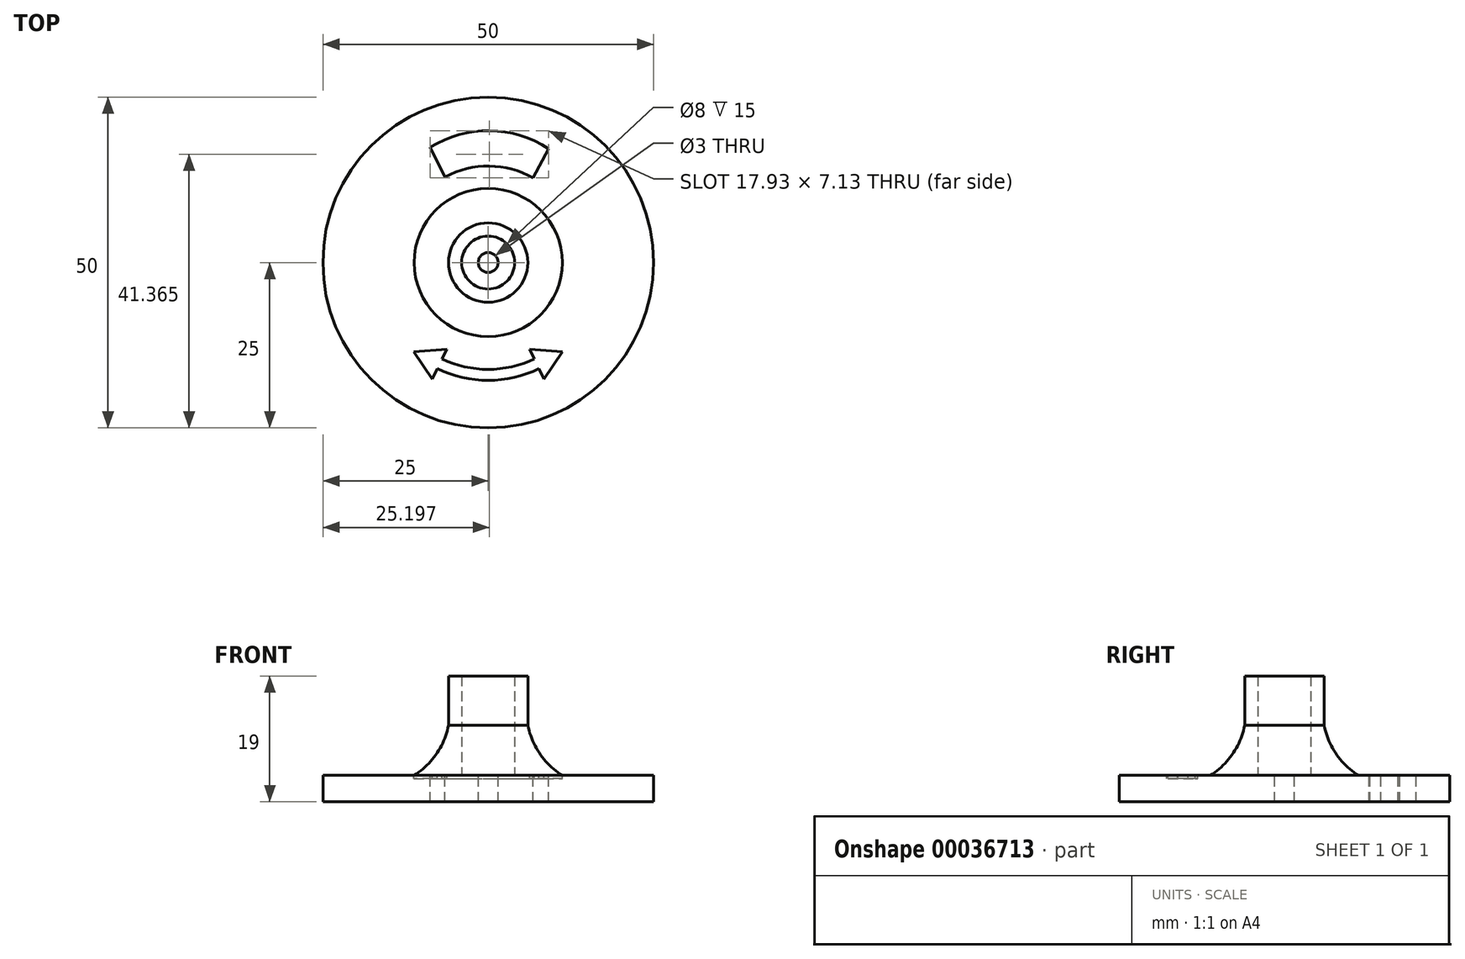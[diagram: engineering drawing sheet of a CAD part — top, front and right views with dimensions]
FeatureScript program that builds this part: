
annotation { "Feature Type Name" : "Feature", "Feature Type Description" : "" }
export const myFeature = defineFeature(function(context is Context, id is Id, definition is map)
    precondition{}
    {
        {
            var Q0;
            Q0=qCreatedBy(makeId("Top.planeOp"),FACE);
            var sketch = newSketch(context, id + "F0", { "sketchPlane" : qUnion([Q0])});
            skCircle(sketch, "E0", {"center": v(0, 0) * mm, "radius": 25 * mm});
            skSolve(sketch);
        }
        {
            var Q0;
            Q0=qCreatedBy(makeId("Top.planeOp"),FACE);
            var sketch = newSketch(context, id + "F1", { "sketchPlane" : qUnion([Q0])});
            skCircle(sketch, "E1", {"center": v(0, 0) * mm, "radius": 6 * mm});
            skCircle(sketch, "E2", {"center": v(0, 0) * mm, "radius": 4 * mm});
            skSolve(sketch);
        }
        {
            var Q0;
            Q0 = qSketchRegion(id + "F0", true);
            extrude(context, id + "F2", {"entities" : qUnion([Q0]), "depth" : 4 * mm});
        }
        {
            var Q0;
            Q0 = qSketchRegion(id + "F1", true);
            extrude(context, id + "F3", {"entities" : qUnion([Q0]), "operationType" : NewBodyOperationType.ADD, "depth" : 19 * mm});
        }
        {
            var Q0;
            {var subQ0=sQuery(id+"F0.wireOp",EDGE,"E0");Q0=makeQuery(id+"F3.boolean.opBoolean","SPLIT",FACE,{"disambiguationData":[TD([makeQuery(id+"F2.opExtrude","SWEPT_FACE",FACE,{"disambiguationData":[OSD([subQ0])]})])],"derivedFrom":makeQuery(id+"F2.opExtrude","CAP_FACE",FACE,{"disambiguationData":[OSD([subQ0])],"isStart":false})});}
            var sketch = newSketch(context, id + "F4", { "sketchPlane" : qUnion([Q0])});
            skCircle(sketch, "E3", {"center": v(0, 0) * mm, "radius": 1.5 * mm});
            skSolve(sketch);
        }
        {
            var Q0;
            Q0=makeQuery(id+"F4.imprint","IMPRINT",FACE,{"disambiguationData":[TD([[makeQuery(id+"F4.imprint","IMPRINT",EDGE,{"derivedFrom":sQuery(id+"F4.wireOp",EDGE,"E3")}),1.0]])]});
            var Q1;
            Q1=sQuery(id+"F4.wireOp",EDGE,"E3");
            extrude(context, id + "F5", {"entities" : qUnion([Q0]), "operationType" : NewBodyOperationType.REMOVE, "surfaceEntities" : qUnion([Q1]), "endBound" : BoundingType.THROUGH_ALL, "oppositeDirection" : true, "depth" : 10 * mm});
        }
        {
            var Q0;
            Q0=qCreatedBy(makeId("Front.planeOp"),FACE);
            var sketch = newSketch(context, id + "F6", { "sketchPlane" : qUnion([Q0])});
            skArc(sketch, "E4", {"start": v(-11.92, 3.58) * mm, "mid": v(-7.42, 7.88) * mm, "end": v(-5.77, 13.88) * mm});
            skLineSegment(sketch, "E5", {"start": v(-11.92, 3.58) * mm, "end": v(-5.77, 3.58) * mm});
            skLineSegment(sketch, "E6", {"start": v(-5.77, 13.88) * mm, "end": v(-5.77, 3.58) * mm});
            skSolve(sketch);
        }
        {
            var Q0;
            Q0=makeQuery(id+"F6.imprint","IMPRINT",FACE,{"disambiguationData":[TD([[makeQuery(id+"F6.imprint","IMPRINT",EDGE,{"derivedFrom":sQuery(id+"F6.wireOp",EDGE,"a2d90b28-1468-49e1-be3c-191cf55d33c0")}),-1.0]])]});
            var Q1;
            Q1=makeQuery(id+"F6.imprint","IMPRINT",FACE,{"disambiguationData":[TD([[makeQuery(id+"F6.imprint","IMPRINT",EDGE,{"derivedFrom":sQuery(id+"F6.wireOp",EDGE,"E4")}),-1.0]])]});
            var Q2;
            Q2=makeQuery(id+"F3.opExtrude","SWEPT_FACE",FACE,{"disambiguationData":[OSD([sQuery(id+"F1.wireOp",EDGE,"E1")])]});
            revolve(context, id + "F7", {"operationType" : NewBodyOperationType.ADD, "entities" : qUnion([Q0, Q1]), "axis" : qUnion([Q2]), "revolveType" : RevolveType.FULL});
        }
        {
            var Q0;
            {var subQ0=sQuery(id+"F0.wireOp",EDGE,"E0");Q0=makeQuery(id+"F3.boolean.opBoolean","SPLIT",FACE,{"disambiguationData":[TD([makeQuery(id+"F2.opExtrude","SWEPT_FACE",FACE,{"disambiguationData":[OSD([subQ0])]})])],"derivedFrom":makeQuery(id+"F2.opExtrude","CAP_FACE",FACE,{"disambiguationData":[OSD([subQ0])],"isStart":false})});}
            var sketch = newSketch(context, id + "F8", { "sketchPlane" : qUnion([Q0])});
            skCircle(sketch, "E7", {"center": v(0, 0) * mm, "radius": 19.5 * mm, "construction": true});
            skCircle(sketch, "E8", {"center": v(0, 0) * mm, "radius": 14.5 * mm, "construction": true});
            skLineSegment(sketch, "E9", {"start": v(0, 0) * mm, "end": v(-8.77, 17.42) * mm});
            skLineSegment(sketch, "E10", {"start": v(-8.77, 17.42) * mm, "end": v(0, 0) * mm});
            skLineSegment(sketch, "E11", {"start": v(0, 0) * mm, "end": v(9.16, 17.21) * mm});
            skArc(sketch, "E12", {"start": v(9.16, 17.21) * mm, "mid": v(0.23, 19.93) * mm, "end": v(-8.77, 17.42) * mm});
            skArc(sketch, "E13", {"start": v(6.81, 12.8) * mm, "mid": v(0.17, 14.58) * mm, "end": v(-6.52, 12.95) * mm});
            skSolve(sketch);
        }
        {
            var Q0;
            {var subQ1=sQuery(id+"F8.wireOp",EDGE,"E12");Q0=makeQuery(id+"F8.imprint","IMPRINT",FACE,{"disambiguationData":[TD([[makeQuery(id+"F8.imprint","IMPRINT",EDGE,{"derivedFrom":subQ1}),1.0]])]});}
            extrude(context, id + "F9", {"entities" : qUnion([Q0]), "operationType" : NewBodyOperationType.REMOVE, "oppositeDirection" : true, "depth" : 25 * mm});
        }
        {
            var Q0;
            Q0=qCreatedBy(makeId("Top.planeOp"),FACE);
            var sketch = newSketch(context, id + "F10", { "sketchPlane" : qUnion([Q0])});
            skLineSegment(sketch, "E14", {"start": v(0, 0) * mm, "end": v(0, 17) * mm, "construction": true});
            skSolve(sketch);
        }
        {
            var Q0;
            {var subQ6=sQuery(id+"F8.wireOp",EDGE,"E12");Q0=makeQuery(id+"F8.imprint","IMPRINT",FACE,{"disambiguationData":[TD([[makeQuery(id+"F8.imprint","IMPRINT",EDGE,{"derivedFrom":subQ6}),-1.0]])]});}
            var sketch = newSketch(context, id + "F11", { "sketchPlane" : qUnion([Q0])});
            skCircle(sketch, "E15.cCircle", {"center": v(-8.65, -14.7) * mm, "radius": 1.44 * mm, "construction": true});
            skLineSegment(sketch, "E15.0", {"start": v(-6.27, -13.08) * mm, "end": v(-6.98, -14.56) * mm});
            skLineSegment(sketch, "E15.1", {"start": v(-8.43, -17.59) * mm, "end": v(-11.25, -13.46) * mm});
            skLineSegment(sketch, "E15.2", {"start": v(-11.25, -13.46) * mm, "end": v(-6.27, -13.08) * mm});
            skPoint(sketch, "E15.0.midPoint", {"position": v(-7.35, -15.33) * mm});
            skLineSegment(sketch, "E16", {"start": v(0, 0) * mm, "end": v(-8.43, -17.59) * mm, "construction": true});
            skLineSegment(sketch, "E17", {"start": v(-7.7, -16.05) * mm, "end": v(-8.43, -17.59) * mm});
            skLineSegment(sketch, "E18", {"start": v(-6.98, -14.56) * mm, "end": v(-7.7, -16.05) * mm});
            skArc(sketch, "E19", {"start": v(-7.7, -16.05) * mm, "mid": v(-3.94, -17.36) * mm, "end": v(0, -17.8) * mm});
            skArc(sketch, "E20", {"start": v(-6.98, -14.56) * mm, "mid": v(-3.58, -15.75) * mm, "end": v(0, -16.15) * mm});
            skLineSegment(sketch, "E21", {"start": v(0, -16.15) * mm, "end": v(0, -17.8) * mm});
            skLineSegment(sketch, "E22", {"start": v(0, 0) * mm, "end": v(0, -19.44) * mm, "construction": true});
            skLineSegment(sketch, "E23.MirrorCS", {"start": v(11.25, -13.46) * mm, "end": v(6.27, -13.08) * mm});
            skLineSegment(sketch, "E24.MirrorCS", {"start": v(6.27, -13.08) * mm, "end": v(6.98, -14.56) * mm});
            skLineSegment(sketch, "E25.MirrorCS", {"start": v(6.98, -14.56) * mm, "end": v(7.7, -16.05) * mm});
            skLineSegment(sketch, "E26.MirrorCS", {"start": v(7.7, -16.05) * mm, "end": v(8.43, -17.59) * mm});
            skLineSegment(sketch, "E27.MirrorCS", {"start": v(8.43, -17.59) * mm, "end": v(11.25, -13.46) * mm});
            skArc(sketch, "E28.MirrorCS", {"start": v(7.7, -16.05) * mm, "mid": v(3.94, -17.36) * mm, "end": v(0, -17.8) * mm});
            skArc(sketch, "E29.MirrorCS", {"start": v(6.98, -14.56) * mm, "mid": v(3.58, -15.75) * mm, "end": v(0, -16.15) * mm});
            skSolve(sketch);
        }
        {
            var Q0;
            Q0=makeQuery(id+"F11.imprint","IMPRINT",FACE,{"disambiguationData":[TD([[makeQuery(id+"F11.imprint","IMPRINT",EDGE,{"derivedFrom":sQuery(id+"F11.wireOp",EDGE,"E15.0")}),-1.0]])]});
            var Q1;
            Q1=makeQuery(id+"F11.imprint","IMPRINT",FACE,{"disambiguationData":[TD([[makeQuery(id+"F11.imprint","IMPRINT",EDGE,{"derivedFrom":sQuery(id+"F11.wireOp",EDGE,"E23.MirrorCS")}),1.0]])]});
            var Q2;
            Q2=makeQuery(id+"F11.imprint","IMPRINT",FACE,{"disambiguationData":[TD([[makeQuery(id+"F11.imprint","IMPRINT",EDGE,{"derivedFrom":sQuery(id+"F11.wireOp",EDGE,"E21")}),1.0]])]});
            var Q3;
            Q3=makeQuery(id+"F11.imprint","IMPRINT",FACE,{"disambiguationData":[TD([[makeQuery(id+"F11.imprint","IMPRINT",EDGE,{"derivedFrom":sQuery(id+"F11.wireOp",EDGE,"E18")}),1.0]])]});
            var Q4;
            Q4 = qSketchRegion(id + "F10", true);
            extrude(context, id + "F12", {"entities" : qUnion([Q0, Q1, Q2, Q3, Q4]), "operationType" : NewBodyOperationType.REMOVE, "oppositeDirection" : true, "depth" : .5 * mm});
        }
    });
